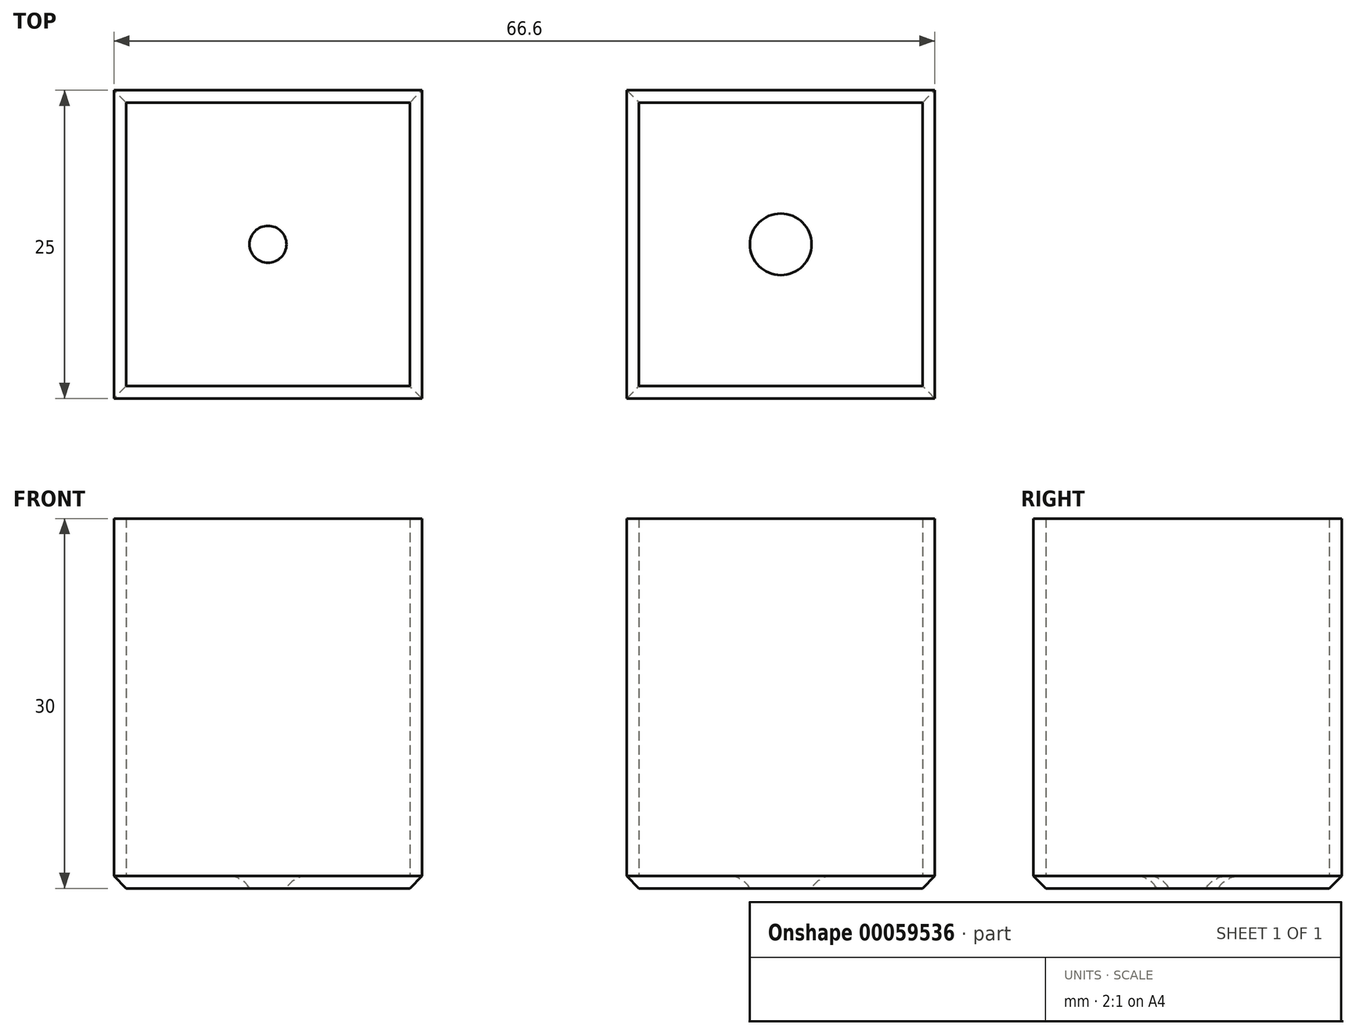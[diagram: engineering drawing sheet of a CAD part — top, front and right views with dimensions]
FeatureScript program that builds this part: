
annotation { "Feature Type Name" : "Feature", "Feature Type Description" : "" }
export const myFeature = defineFeature(function(context is Context, id is Id, definition is map)
    precondition{}
    {
        {
            var Q0;
            Q0=qCreatedBy(makeId("Top.planeOp"),FACE);
            var sketch = newSketch(context, id + "F0", { "sketchPlane" : qUnion([Q0])});
            skLineSegment(sketch, "E0.rect.bottom", {"start": v(12.5, -12.5) * mm, "end": v(-12.5, -12.5) * mm});
            skLineSegment(sketch, "E0.rect.top", {"start": v(12.5, 12.5) * mm, "end": v(-12.5, 12.5) * mm});
            skLineSegment(sketch, "E0.rect.left", {"start": v(12.5, -12.5) * mm, "end": v(12.5, 12.5) * mm});
            skLineSegment(sketch, "E0.rect.right", {"start": v(-12.5, -12.5) * mm, "end": v(-12.5, 12.5) * mm});
            skPoint(sketch, "E0.rect.middle", {"position": v(0, 0) * mm});
            skSolve(sketch);
        }
        {
            var Q0;
            Q0=makeQuery(id+"F0.imprint","IMPRINT",FACE,{"disambiguationData":[TD([[makeQuery(id+"F0.imprint","IMPRINT",EDGE,{"derivedFrom":sQuery(id+"F0.wireOp",EDGE,"E0.rect.bottom")}),-1.0]])]});
            extrude(context, id + "F1", {"entities" : qUnion([Q0]), "depth" : 30 * mm});
        }
        {
            var Q0;
            Q0=makeQuery(id+"F1.opExtrude","CAP_FACE",FACE,{"disambiguationData":[OSD([sQuery(id+"F0.wireOp",EDGE,"E0.rect.bottom"),sQuery(id+"F0.wireOp",EDGE,"E0.rect.top"),sQuery(id+"F0.wireOp",EDGE,"E0.rect.left"),sQuery(id+"F0.wireOp",EDGE,"E0.rect.right")])],"isStart":false});
            shell(context, id + "F2", {"entities" : qUnion([Q0]), "thickness" : 1 * mm});
        }
        {
            var Q0;
            Q0=makeQuery(id+"F1.opExtrude","SWEPT_BODY",BODY,{"disambiguationData":[OSD([sQuery(id+"F0.wireOp",EDGE,"E0.rect.bottom"),sQuery(id+"F0.wireOp",EDGE,"E0.rect.top"),sQuery(id+"F0.wireOp",EDGE,"E0.rect.left"),sQuery(id+"F0.wireOp",EDGE,"E0.rect.right")])]});
            var Q1;
            Q1=qCreatedBy(makeId("Right.planeOp"),FACE);
            transform(context, id + "F3", {"entities" : qUnion([Q0]), "transformType" : TransformType.TRANSLATION_DISTANCE, "transformDirection" : qUnion([Q1]), "distance" : 41.6 * mm, "makeCopy" : true});
        }
        {
            var Q0;
            Q0=makeQuery(id+"F1.opExtrude","CAP_FACE",FACE,{"disambiguationData":[OSD([sQuery(id+"F0.wireOp",EDGE,"E0.rect.bottom"),sQuery(id+"F0.wireOp",EDGE,"E0.rect.top"),sQuery(id+"F0.wireOp",EDGE,"E0.rect.left"),sQuery(id+"F0.wireOp",EDGE,"E0.rect.right")])],"isStart":true});
            var sketch = newSketch(context, id + "F4", { "sketchPlane" : qUnion([Q0])});
            skCircle(sketch, "E1", {"center": v(0, 0) * mm, "radius": 1.5 * mm});
            skLineSegment(sketch, "E2", {"start": v(29.1, -12.5) * mm, "end": v(54.1, 12.5) * mm, "construction": true});
            skCircle(sketch, "E3", {"center": v(41.6, 0) * mm, "radius": 2.5 * mm});
            skSolve(sketch);
        }
        {
            var Q0;
            Q0 = qSketchRegion(id + "F4", true);
            extrude(context, id + "F5", {"entities" : qUnion([Q0]), "operationType" : NewBodyOperationType.REMOVE, "endBound" : BoundingType.THROUGH_ALL, "oppositeDirection" : true, "depth" : 25 * mm});
        }
        {
            var Q0;
            Q0=makeQuery(id+"F5.boolean.opBoolean","INTERSECT",EDGE,{"derivedFrom":[makeQuery(id+"F2.opShell","OFFSET_FACE",FACE,{"disambiguationData":[OSD([sQuery(id+"F0.wireOp",EDGE,"E0.rect.bottom"),sQuery(id+"F0.wireOp",EDGE,"E0.rect.top"),sQuery(id+"F0.wireOp",EDGE,"E0.rect.left"),sQuery(id+"F0.wireOp",EDGE,"E0.rect.right")])]}),makeQuery(id+"F5.opExtrude","SWEPT_FACE",FACE,{"disambiguationData":[OSD([sQuery(id+"F4.wireOp",EDGE,"E1")])]})]});
            var Q1;
            Q1=makeQuery(id+"F5.boolean.opBoolean","INTERSECT",EDGE,{"derivedFrom":[makeQuery(id+"F3.opPattern","COPY",FACE,{"derivedFrom":makeQuery(id+"F2.opShell","OFFSET_FACE",FACE,{"disambiguationData":[OSD([sQuery(id+"F0.wireOp",EDGE,"E0.rect.bottom"),sQuery(id+"F0.wireOp",EDGE,"E0.rect.top"),sQuery(id+"F0.wireOp",EDGE,"E0.rect.left"),sQuery(id+"F0.wireOp",EDGE,"E0.rect.right")])]}),"instanceName":"1"}),makeQuery(id+"F5.opExtrude","SWEPT_FACE",FACE,{"disambiguationData":[OSD([sQuery(id+"F4.wireOp",EDGE,"E3")])]})]});
            fillet(context, id + "F6", {"entities" : qUnion([Q0, Q1]), "radius" : 2 * mm, "tangentPropagation" : true, "allowEdgeOverflow" : false});
        }
        {
            var Q0;
            Q0=makeQuery(id+"F1.opExtrude","CAP_EDGE",EDGE,{"disambiguationData":[OSD([sQuery(id+"F0.wireOp",EDGE,"E0.rect.right")])],"isStart":true});
            var Q1;
            Q1=makeQuery(id+"F1.opExtrude","CAP_EDGE",EDGE,{"disambiguationData":[OSD([sQuery(id+"F0.wireOp",EDGE,"E0.rect.top")])],"isStart":true});
            var Q2;
            Q2=makeQuery(id+"F1.opExtrude","CAP_EDGE",EDGE,{"disambiguationData":[OSD([sQuery(id+"F0.wireOp",EDGE,"E0.rect.left")])],"isStart":true});
            var Q3;
            Q3=makeQuery(id+"F1.opExtrude","CAP_EDGE",EDGE,{"disambiguationData":[OSD([sQuery(id+"F0.wireOp",EDGE,"E0.rect.bottom")])],"isStart":true});
            var Q4;
            Q4=makeQuery(id+"F3.opPattern","COPY",EDGE,{"derivedFrom":makeQuery(id+"F1.opExtrude","CAP_EDGE",EDGE,{"disambiguationData":[OSD([sQuery(id+"F0.wireOp",EDGE,"E0.rect.bottom")])],"isStart":true}),"instanceName":"1"});
            var Q5;
            Q5=makeQuery(id+"F3.opPattern","COPY",EDGE,{"derivedFrom":makeQuery(id+"F1.opExtrude","CAP_EDGE",EDGE,{"disambiguationData":[OSD([sQuery(id+"F0.wireOp",EDGE,"E0.rect.right")])],"isStart":true}),"instanceName":"1"});
            var Q6;
            Q6=makeQuery(id+"F3.opPattern","COPY",EDGE,{"derivedFrom":makeQuery(id+"F1.opExtrude","CAP_EDGE",EDGE,{"disambiguationData":[OSD([sQuery(id+"F0.wireOp",EDGE,"E0.rect.left")])],"isStart":true}),"instanceName":"1"});
            var Q7;
            Q7=makeQuery(id+"F3.opPattern","COPY",EDGE,{"derivedFrom":makeQuery(id+"F1.opExtrude","CAP_EDGE",EDGE,{"disambiguationData":[OSD([sQuery(id+"F0.wireOp",EDGE,"E0.rect.top")])],"isStart":true}),"instanceName":"1"});
            chamfer(context, id + "F7", {"entities" : qUnion([Q0, Q1, Q2, Q3, Q4, Q5, Q6, Q7]), "width" : 1 * mm, "tangentPropagation" : true});
        }
    });
